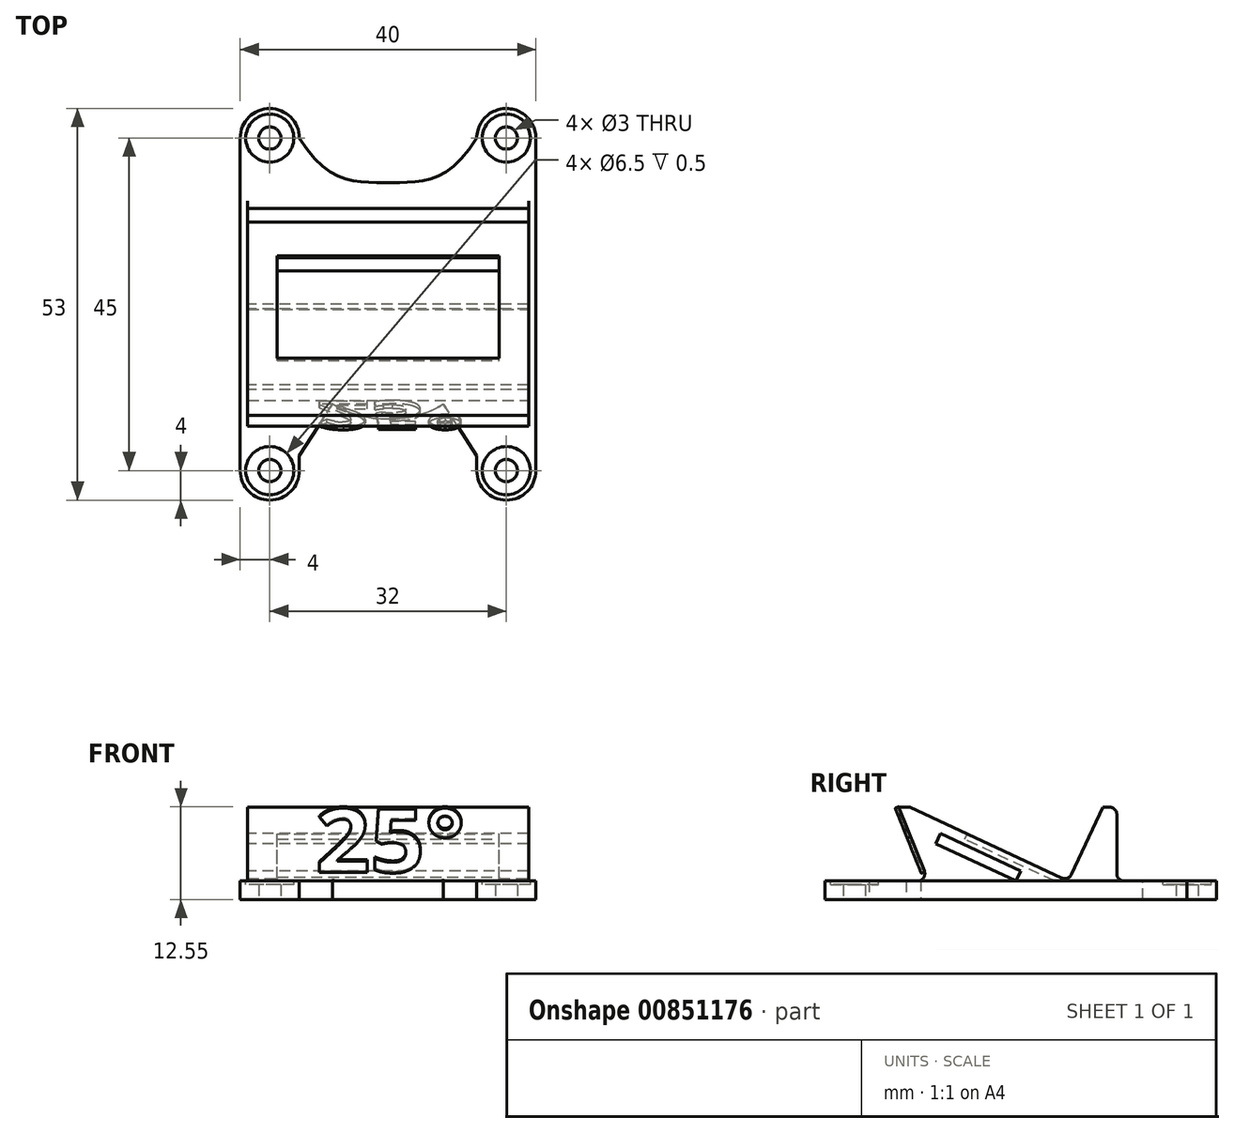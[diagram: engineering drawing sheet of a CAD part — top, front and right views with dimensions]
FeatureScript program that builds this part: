
annotation { "Feature Type Name" : "Feature", "Feature Type Description" : "" }
export const myFeature = defineFeature(function(context is Context, id is Id, definition is map)
    precondition{}
    {
        {
            var Q0;
            Q0=qCreatedBy(makeId("Top.planeOp"),FACE);
            var sketch = newSketch(context, id + "F0", { "sketchPlane" : qUnion([Q0])});
            skCircle(sketch, "E0", {"center": v(-16, 22.5) * mm, "radius": 4 * mm});
            skCircle(sketch, "E1", {"center": v(16, 22.5) * mm, "radius": 4 * mm});
            skCircle(sketch, "E2", {"center": v(-16, -22.5) * mm, "radius": 4 * mm});
            skCircle(sketch, "E3", {"center": v(16, -22.5) * mm, "radius": 4 * mm});
            skLineSegment(sketch, "E4", {"start": v(-20, 22.5) * mm, "end": v(-20, -22.5) * mm});
            skLineSegment(sketch, "E5", {"start": v(20, 22.55) * mm, "end": v(20, -22.5) * mm});
            skLineSegment(sketch, "E6", {"start": v(-12, -22.5) * mm, "end": v(-12, -20.5) * mm});
            skLineSegment(sketch, "E7", {"start": v(12, -22.5) * mm, "end": v(12, -20.5) * mm});
            skLineSegment(sketch, "E8", {"start": v(-12, -20.5) * mm, "end": v(-7.5, -13.5) * mm});
            skLineSegment(sketch, "E9", {"start": v(12, -20.5) * mm, "end": v(7.5, -13.5) * mm});
            skFitSpline(sketch, "E10", {"points": [v(-7.5, -13.5) * mm, v(0, -15.5) * mm, v(7.5, -13.5) * mm], "startDerivative": vector(15, -9) * mm, "endDerivative": vector(15, 9) * mm});
            skFitSpline(sketch, "E11", {"points": [v(-12, 22.5) * mm, v(0, 16.5) * mm, v(12, 22.5) * mm], "startDerivative": vector(24, -39) * mm, "endDerivative": vector(24, 39) * mm});
            skSolve(sketch);
        }
        {
            var Q0;
            Q0=qSketchRegion(id+"F0",true);
            extrude(context, id + "F1", {"entities" : qUnion([Q0]), "depth" : 2.5 * mm, "offsetDistance" : 25 * mm});
        }
        {
            var Q0;
            Q0=qCreatedBy(makeId("Right.planeOp"),FACE);
            var sketch = newSketch(context, id + "F2", { "sketchPlane" : qUnion([Q0])});
            skLineSegment(sketch, "E12", {"start": v(13, 10.16) * mm, "end": v(13, 2.5) * mm});
            skLineSegment(sketch, "E13", {"start": v(13, 2.5) * mm, "end": v(-12.5, 2.5) * mm});
            skLineSegment(sketch, "E14", {"start": v(-12.5, 2.5) * mm, "end": v(-16.5, 12.5) * mm});
            skLineSegment(sketch, "E15", {"start": v(-16.5, 12.5) * mm, "end": v(13, 12.5) * mm});
            skLineSegment(sketch, "E16", {"start": v(13, 12.5) * mm, "end": v(13, 10.16) * mm});
            skSolve(sketch);
        }
        {
            var Q0;
            Q0=qSketchRegion(id+"F2",true);
            extrude(context, id + "F3", {"entities" : qUnion([Q0]), "endBound" : BoundingType.SYMMETRIC, "depth" : 38 * mm, "offsetDistance" : 25 * mm});
        }
        {
            var Q0;
            Q0=makeQuery(id+"F3.opExtrude","CAP_FACE",FACE,{"disambiguationData":[OSD([sQuery(id+"F2.wireOp",EDGE,"E12"),sQuery(id+"F2.wireOp",EDGE,"E13"),sQuery(id+"F2.wireOp",EDGE,"E14"),sQuery(id+"F2.wireOp",EDGE,"E15"),sQuery(id+"F2.wireOp",EDGE,"E16")])],"isStart":true});
            var sketch = newSketch(context, id + "F4", { "sketchPlane" : qUnion([Q0])});
            skLineSegment(sketch, "E17", {"start": v(-11.1, 12.5) * mm, "end": v(-6.45, 2.5) * mm});
            skLineSegment(sketch, "E18", {"start": v(-6.45, 2.5) * mm, "end": v(15, 12.5) * mm});
            skLineSegment(sketch, "E19", {"start": v(15, 12.5) * mm, "end": v(-11.1, 12.5) * mm});
            skSolve(sketch);
        }
        {
            var Q0;
            Q0=qSketchRegion(id+"F4",true);
            extrude(context, id + "F5", {"entities" : qUnion([Q0]), "oppositeDirection" : true, "depth" : 40 * mm, "offsetDistance" : 25 * mm});
        }
        {
            var Q0;
            Q0=makeQuery(id+"F5.opExtrude","SWEPT_BODY",BODY,{"disambiguationData":[OSD([sQuery(id+"F4.wireOp",EDGE,"E17"),sQuery(id+"F4.wireOp",EDGE,"E18"),sQuery(id+"F4.wireOp",EDGE,"E19")])]});
            var Q1;
            Q1=makeQuery(id+"F3.opExtrude","SWEPT_BODY",BODY,{"disambiguationData":[OSD([sQuery(id+"F2.wireOp",EDGE,"E12"),sQuery(id+"F2.wireOp",EDGE,"E13"),sQuery(id+"F2.wireOp",EDGE,"E14"),sQuery(id+"F2.wireOp",EDGE,"E15"),sQuery(id+"F2.wireOp",EDGE,"E16")])]});
            booleanBodies(context, id + "F6", {"operationType" : BooleanOperationType.SUBTRACTION, "tools" : qUnion([Q0]), "targets" : qUnion([Q1])});
        }
        {
            var Q0;
            Q0=sQuery(id+"F0.wireOp",VERTEX,"E0.center");
            var Q1;
            Q1=sQuery(id+"F0.wireOp",VERTEX,"E1.center");
            var Q2;
            Q2=sQuery(id+"F0.wireOp",VERTEX,"E2.center");
            var Q3;
            Q3=sQuery(id+"F0.wireOp",VERTEX,"E3.center");
            var Q4;
            Q4=makeQuery(id+"F1.opExtrude","SWEPT_BODY",BODY,{"disambiguationData":[OSD([sQuery(id+"F0.wireOp",EDGE,"E0"),sQuery(id+"F0.wireOp",EDGE,"E1"),sQuery(id+"F0.wireOp",EDGE,"E2"),sQuery(id+"F0.wireOp",EDGE,"E3"),sQuery(id+"F0.wireOp",EDGE,"E4"),sQuery(id+"F0.wireOp",EDGE,"E5"),sQuery(id+"F0.wireOp",EDGE,"E6"),sQuery(id+"F0.wireOp",EDGE,"E7"),sQuery(id+"F0.wireOp",EDGE,"E8"),sQuery(id+"F0.wireOp",EDGE,"E9"),sQuery(id+"F0.wireOp",EDGE,"E10"),sQuery(id+"F0.wireOp",EDGE,"E11")])]});
            hole(context, id + "F7", {"style" : HoleStyle.SIMPLE, "endStyle" : HoleEndStyle.THROUGH, "oppositeDirection" : true, "holeDiameter" : 3 * mm, "tappedDepth" : 12 * mm, "tapClearance" : 3, "locations" : qUnion([Q0, Q1, Q2, Q3]), "scope" : qUnion([Q4])});
        }
        {
            var Q0;
            Q0=makeQuery(id+"F1.opExtrude","CAP_FACE",FACE,{"disambiguationData":[OSD([sQuery(id+"F0.wireOp",EDGE,"E0"),sQuery(id+"F0.wireOp",EDGE,"E1"),sQuery(id+"F0.wireOp",EDGE,"E2"),sQuery(id+"F0.wireOp",EDGE,"E3"),sQuery(id+"F0.wireOp",EDGE,"E4"),sQuery(id+"F0.wireOp",EDGE,"E5"),sQuery(id+"F0.wireOp",EDGE,"E6"),sQuery(id+"F0.wireOp",EDGE,"E7"),sQuery(id+"F0.wireOp",EDGE,"E8"),sQuery(id+"F0.wireOp",EDGE,"E9"),sQuery(id+"F0.wireOp",EDGE,"E10"),sQuery(id+"F0.wireOp",EDGE,"E11")])],"isStart":false});
            var sketch = newSketch(context, id + "F8", { "sketchPlane" : qUnion([Q0])});
            skCircle(sketch, "E20", {"center": v(-16, 22.5) * mm, "radius": 3.25 * mm});
            skCircle(sketch, "E21", {"center": v(16, 22.5) * mm, "radius": 3.25 * mm});
            skCircle(sketch, "E22", {"center": v(-16, -22.5) * mm, "radius": 3.25 * mm});
            skCircle(sketch, "E23", {"center": v(16, -22.5) * mm, "radius": 3.25 * mm});
            skSolve(sketch);
        }
        {
            var Q0;
            Q0=qSketchRegion(id+"F8",true);
            extrude(context, id + "F9", {"entities" : qUnion([Q0]), "oppositeDirection" : true, "depth" : 0.5 * mm, "offsetDistance" : 25 * mm});
        }
        {
            var Q0;
            Q0=makeQuery(id+"F9.opExtrude","SWEPT_BODY",BODY,{"disambiguationData":[OSD([sQuery(id+"F8.wireOp",EDGE,"E20")])]});
            var Q1;
            Q1=makeQuery(id+"F9.opExtrude","SWEPT_BODY",BODY,{"disambiguationData":[OSD([sQuery(id+"F8.wireOp",EDGE,"E21")])]});
            var Q2;
            Q2=makeQuery(id+"F9.opExtrude","SWEPT_BODY",BODY,{"disambiguationData":[OSD([sQuery(id+"F8.wireOp",EDGE,"E22")])]});
            var Q3;
            Q3=makeQuery(id+"F9.opExtrude","SWEPT_BODY",BODY,{"disambiguationData":[OSD([sQuery(id+"F8.wireOp",EDGE,"E23")])]});
            var Q4;
            Q4=makeQuery(id+"F1.opExtrude","SWEPT_BODY",BODY,{"disambiguationData":[OSD([sQuery(id+"F0.wireOp",EDGE,"E0"),sQuery(id+"F0.wireOp",EDGE,"E1"),sQuery(id+"F0.wireOp",EDGE,"E2"),sQuery(id+"F0.wireOp",EDGE,"E3"),sQuery(id+"F0.wireOp",EDGE,"E4"),sQuery(id+"F0.wireOp",EDGE,"E5"),sQuery(id+"F0.wireOp",EDGE,"E6"),sQuery(id+"F0.wireOp",EDGE,"E7"),sQuery(id+"F0.wireOp",EDGE,"E8"),sQuery(id+"F0.wireOp",EDGE,"E9"),sQuery(id+"F0.wireOp",EDGE,"E10"),sQuery(id+"F0.wireOp",EDGE,"E11")])]});
            booleanBodies(context, id + "F10", {"operationType" : BooleanOperationType.SUBTRACTION, "tools" : qUnion([Q0, Q1, Q2, Q3]), "targets" : qUnion([Q4])});
        }
        {
            var Q0;
            Q0=makeQuery(id+"F6.opBoolean","COPY",FACE,{"derivedFrom":makeQuery(id+"F5.opExtrude","SWEPT_FACE",FACE,{"disambiguationData":[OSD([sQuery(id+"F4.wireOp",EDGE,"E18")])]})});
            var sketch = newSketch(context, id + "F11", { "sketchPlane" : qUnion([Q0])});
            skLineSegment(sketch, "E24.bottom", {"start": v(-15, 4.67) * mm, "end": v(15, 4.67) * mm});
            skLineSegment(sketch, "E24.top", {"start": v(-15, -10.33) * mm, "end": v(15, -10.33) * mm});
            skLineSegment(sketch, "E24.left", {"start": v(-15, 4.67) * mm, "end": v(-15, -10.33) * mm});
            skLineSegment(sketch, "E24.right", {"start": v(15, 4.67) * mm, "end": v(15, -10.33) * mm});
            skSolve(sketch);
        }
        {
            var Q0;
            Q0=qSketchRegion(id+"F11",true);
            extrude(context, id + "F12", {"entities" : qUnion([Q0]), "oppositeDirection" : true, "depth" : 0.8 * mm, "offsetDistance" : 25 * mm});
        }
        {
            var Q0;
            Q0=makeQuery(id+"F12.opExtrude","SWEPT_BODY",BODY,{"disambiguationData":[OSD([sQuery(id+"F11.wireOp",EDGE,"E24.bottom"),sQuery(id+"F11.wireOp",EDGE,"E24.top"),sQuery(id+"F11.wireOp",EDGE,"E24.left"),sQuery(id+"F11.wireOp",EDGE,"E24.right")])]});
            var Q1;
            Q1=makeQuery(id+"F6.opBoolean","SPLIT",BODY,{"disambiguationData":[OD(1.0)],"derivedFrom":makeQuery(id+"F3.opExtrude","SWEPT_BODY",BODY,{"disambiguationData":[OSD([sQuery(id+"F2.wireOp",EDGE,"E12"),sQuery(id+"F2.wireOp",EDGE,"E13"),sQuery(id+"F2.wireOp",EDGE,"E14"),sQuery(id+"F2.wireOp",EDGE,"E15"),sQuery(id+"F2.wireOp",EDGE,"E16")])]})});
            booleanBodies(context, id + "F13", {"operationType" : BooleanOperationType.SUBTRACTION, "tools" : qUnion([Q0]), "targets" : qUnion([Q1])});
        }
        {
            var Q0;
            {var subQ0=sQuery(id+"F2.wireOp",EDGE,"E13");var subQ1=sQuery(id+"F2.wireOp",EDGE,"E14");Q0=makeQuery(id+"F6.opBoolean","SPLIT",FACE,{"disambiguationData":[TD([makeQuery(id+"F3.opExtrude","SWEPT_FACE",FACE,{"disambiguationData":[OSD([subQ1])]})])],"derivedFrom":makeQuery(id+"F3.opExtrude","CAP_FACE",FACE,{"disambiguationData":[OSD([sQuery(id+"F2.wireOp",EDGE,"E12"),subQ0,subQ1,sQuery(id+"F2.wireOp",EDGE,"E15"),sQuery(id+"F2.wireOp",EDGE,"E16")])],"isStart":true})});}
            var sketch = newSketch(context, id + "F14", { "sketchPlane" : qUnion([Q0])});
            skLineSegment(sketch, "E25", {"start": v(0, 3.85) * mm, "end": v(10.88, 8.92) * mm});
            skLineSegment(sketch, "E26", {"start": v(10.88, 8.92) * mm, "end": v(11.5, 7.56) * mm});
            skLineSegment(sketch, "E27", {"start": v(11.5, 7.56) * mm, "end": v(0.63, 2.5) * mm});
            skLineSegment(sketch, "E28", {"start": v(0.63, 2.5) * mm, "end": v(0, 3.85) * mm});
            skSolve(sketch);
        }
        {
            var Q0;
            Q0=qSketchRegion(id+"F14",true);
            extrude(context, id + "F15", {"entities" : qUnion([Q0]), "oppositeDirection" : true, "depth" : 40 * mm, "offsetDistance" : 25 * mm});
        }
        {
            var Q0;
            Q0=makeQuery(id+"F15.opExtrude","SWEPT_BODY",BODY,{"disambiguationData":[OSD([sQuery(id+"F14.wireOp",EDGE,"E25"),sQuery(id+"F14.wireOp",EDGE,"E26"),sQuery(id+"F14.wireOp",EDGE,"E27"),sQuery(id+"F14.wireOp",EDGE,"E28")])]});
            var Q1;
            Q1=makeQuery(id+"F6.opBoolean","SPLIT",BODY,{"disambiguationData":[OD(1.0)],"derivedFrom":makeQuery(id+"F3.opExtrude","SWEPT_BODY",BODY,{"disambiguationData":[OSD([sQuery(id+"F2.wireOp",EDGE,"E12"),sQuery(id+"F2.wireOp",EDGE,"E13"),sQuery(id+"F2.wireOp",EDGE,"E14"),sQuery(id+"F2.wireOp",EDGE,"E15"),sQuery(id+"F2.wireOp",EDGE,"E16")])]})});
            booleanBodies(context, id + "F16", {"operationType" : BooleanOperationType.SUBTRACTION, "tools" : qUnion([Q0]), "targets" : qUnion([Q1])});
        }
        {
            var Q0;
            Q0=makeQuery(id+"F1.opExtrude","SWEPT_BODY",BODY,{"disambiguationData":[OSD([sQuery(id+"F0.wireOp",EDGE,"E0"),sQuery(id+"F0.wireOp",EDGE,"E1"),sQuery(id+"F0.wireOp",EDGE,"E2"),sQuery(id+"F0.wireOp",EDGE,"E3"),sQuery(id+"F0.wireOp",EDGE,"E4"),sQuery(id+"F0.wireOp",EDGE,"E5"),sQuery(id+"F0.wireOp",EDGE,"E6"),sQuery(id+"F0.wireOp",EDGE,"E7"),sQuery(id+"F0.wireOp",EDGE,"E8"),sQuery(id+"F0.wireOp",EDGE,"E9"),sQuery(id+"F0.wireOp",EDGE,"E10"),sQuery(id+"F0.wireOp",EDGE,"E11")])]});
            var Q1;
            Q1=makeQuery(id+"F6.opBoolean","SPLIT",BODY,{"disambiguationData":[OD(0.0)],"derivedFrom":makeQuery(id+"F3.opExtrude","SWEPT_BODY",BODY,{"disambiguationData":[OSD([sQuery(id+"F2.wireOp",EDGE,"E12"),sQuery(id+"F2.wireOp",EDGE,"E13"),sQuery(id+"F2.wireOp",EDGE,"E14"),sQuery(id+"F2.wireOp",EDGE,"E15"),sQuery(id+"F2.wireOp",EDGE,"E16")])]})});
            var Q2;
            Q2=makeQuery(id+"F6.opBoolean","SPLIT",BODY,{"disambiguationData":[OD(1.0)],"derivedFrom":makeQuery(id+"F3.opExtrude","SWEPT_BODY",BODY,{"disambiguationData":[OSD([sQuery(id+"F2.wireOp",EDGE,"E12"),sQuery(id+"F2.wireOp",EDGE,"E13"),sQuery(id+"F2.wireOp",EDGE,"E14"),sQuery(id+"F2.wireOp",EDGE,"E15"),sQuery(id+"F2.wireOp",EDGE,"E16")])]})});
            booleanBodies(context, id + "F17", {"operationType" : BooleanOperationType.UNION, "tools" : qUnion([Q0, Q1, Q2])});
        }
        {
            var Q0;
            Q0=makeQuery(id+"F3.opExtrude","SWEPT_EDGE",EDGE,{"disambiguationData":[OSD([sQuery(id+"F2.wireOp",EDGE,"E13"),sQuery(id+"F2.wireOp",EDGE,"E14")])]});
            var Q1;
            Q1=makeQuery(id+"F3.opExtrude","SWEPT_EDGE",EDGE,{"disambiguationData":[OSD([sQuery(id+"F2.wireOp",EDGE,"E15"),sQuery(id+"F2.wireOp",EDGE,"E16")])]});
            var Q2;
            {var subQ0=sQuery(id+"F2.wireOp",EDGE,"E13");var subQ2=sQuery(id+"F4.wireOp",EDGE,"E18");var subQ3=sQuery(id+"F4.wireOp",EDGE,"E17");var subQ4=makeQuery(id+"F5.opExtrude","SWEPT_EDGE",EDGE,{"disambiguationData":[OSD([subQ0,subQ3,subQ2])]});Q2=makeQuery(id+"F17.opBoolean","MERGE",EDGE,{"derivedFrom":[makeQuery(id+"F6.opBoolean","COPY",EDGE,{"disambiguationData":[topologyDisambiguationEdgeConnected([makeQuery(id+"F5.opExtrude","SWEPT_FACE",FACE,{"disambiguationData":[OSD([subQ3])]})])],"derivedFrom":subQ4}),makeQuery(id+"F6.opBoolean","COPY",EDGE,{"disambiguationData":[topologyDisambiguationEdgeConnected([makeQuery(id+"F5.opExtrude","SWEPT_FACE",FACE,{"disambiguationData":[OSD([subQ2])]})])],"derivedFrom":subQ4})]});}
            var Q3;
            Q3=makeQuery(id+"F3.opExtrude","SWEPT_EDGE",EDGE,{"disambiguationData":[OSD([sQuery(id+"F2.wireOp",EDGE,"E12"),sQuery(id+"F2.wireOp",EDGE,"E13")])]});
            fillet(context, id + "F18", {"entities" : qUnion([Q0, Q1, Q2, Q3]), "radius" : 1 * mm, "tangentPropagation" : true, "allowEdgeOverflow" : false});
        }
        {
            var Q0;
            Q0=makeQuery(id+"F3.opExtrude","SWEPT_FACE",FACE,{"disambiguationData":[OSD([sQuery(id+"F2.wireOp",EDGE,"E14")])]});
            var sketch = newSketch(context, id + "F19", { "sketchPlane" : qUnion([Q0])});
            skText(sketch, "E29", { "text": "25°", "fontName": "OpenSans-Bold.ttf"});
            const initialGuessF19  = {"E29": [-0.0098, 0.00844, 1, 0, 0.0093]};
            skSetInitialGuess(sketch, initialGuessF19);
            skSolve(sketch);
        }
        {
            var Q0;
            Q0 = qSketchRegion(id + "F19", true);
            extrude(context, id + "F20", {"entities" : qUnion([Q0]), "operationType" : NewBodyOperationType.ADD, "depth" : 0.5 * mm, "offsetDistance" : 25 * mm});
        }
    });
